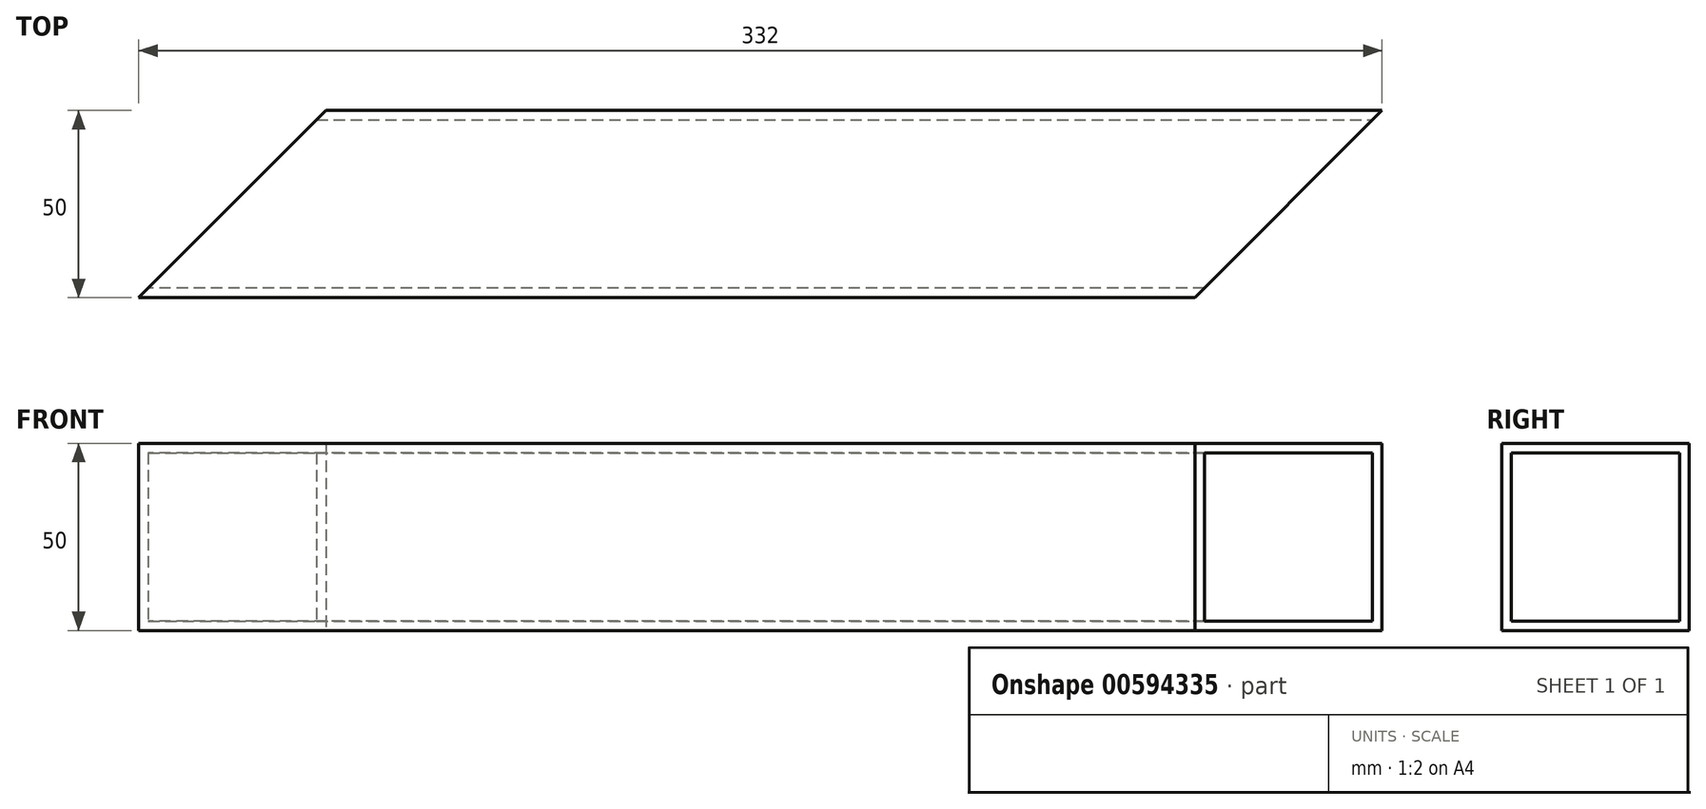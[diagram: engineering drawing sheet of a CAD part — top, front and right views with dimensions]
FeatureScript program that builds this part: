
annotation { "Feature Type Name" : "Feature", "Feature Type Description" : "" }
export const myFeature = defineFeature(function(context is Context, id is Id, definition is map)
    precondition{}
    {
        {
            var Q0;
            Q0=qCreatedBy(makeId("Top.planeOp"),FACE);
            var sketch = newSketch(context, id + "F0", { "sketchPlane" : qUnion([Q0])});
            skLineSegment(sketch, "E0.bottom", {"start": v(116, -25) * mm, "end": v(-116, -25) * mm});
            skLineSegment(sketch, "E0.top", {"start": v(116, 25) * mm, "end": v(-116, 25) * mm});
            skLineSegment(sketch, "E0.left", {"start": v(116, -25) * mm, "end": v(116, 25) * mm});
            skLineSegment(sketch, "E0.right", {"start": v(-116, -25) * mm, "end": v(-116, 25) * mm});
            skPoint(sketch, "E0.middle", {"position": v(0, 0) * mm});
            skLineSegment(sketch, "E1", {"start": v(-116, -25) * mm, "end": v(-166, -25) * mm});
            skLineSegment(sketch, "E2", {"start": v(-166, -25) * mm, "end": v(-116, 25) * mm});
            skLineSegment(sketch, "E3", {"start": v(116, 25) * mm, "end": v(166, 25) * mm});
            skLineSegment(sketch, "E4", {"start": v(166, 25) * mm, "end": v(116, -25) * mm});
            skSolve(sketch);
        }
        {
            var Q0;
            Q0=makeQuery(id+"F0.imprint","IMPRINT",FACE,{"disambiguationData":[TD([[makeQuery(id+"F0.imprint","IMPRINT",EDGE,{"derivedFrom":sQuery(id+"F0.wireOp",EDGE,"E0.left")}),-1.0]])]});
            var Q1;
            Q1=makeQuery(id+"F0.imprint","IMPRINT",FACE,{"disambiguationData":[TD([[makeQuery(id+"F0.imprint","IMPRINT",EDGE,{"derivedFrom":sQuery(id+"F0.wireOp",EDGE,"E0.bottom")}),-1.0]])]});
            var Q2;
            Q2=makeQuery(id+"F0.imprint","IMPRINT",FACE,{"disambiguationData":[TD([[makeQuery(id+"F0.imprint","IMPRINT",EDGE,{"derivedFrom":sQuery(id+"F0.wireOp",EDGE,"E0.right")}),1.0]])]});
            extrude(context, id + "F1", {"entities" : qUnion([Q0, Q1, Q2]), "depth" : 50 * mm, "offsetDistance" : 25.4 * mm});
        }
        {
            var Q0;
            Q0=makeQuery(id+"F1.opExtrude","SWEPT_FACE",FACE,{"disambiguationData":[OSD([sQuery(id+"F0.wireOp",EDGE,"E4")])]});
            var Q1;
            Q1=makeQuery(id+"F1.opExtrude","SWEPT_FACE",FACE,{"disambiguationData":[OSD([sQuery(id+"F0.wireOp",EDGE,"E2")])]});
            shell(context, id + "F2", {"entities" : qUnion([Q0, Q1]), "thickness" : 2.54 * mm});
        }
    });
